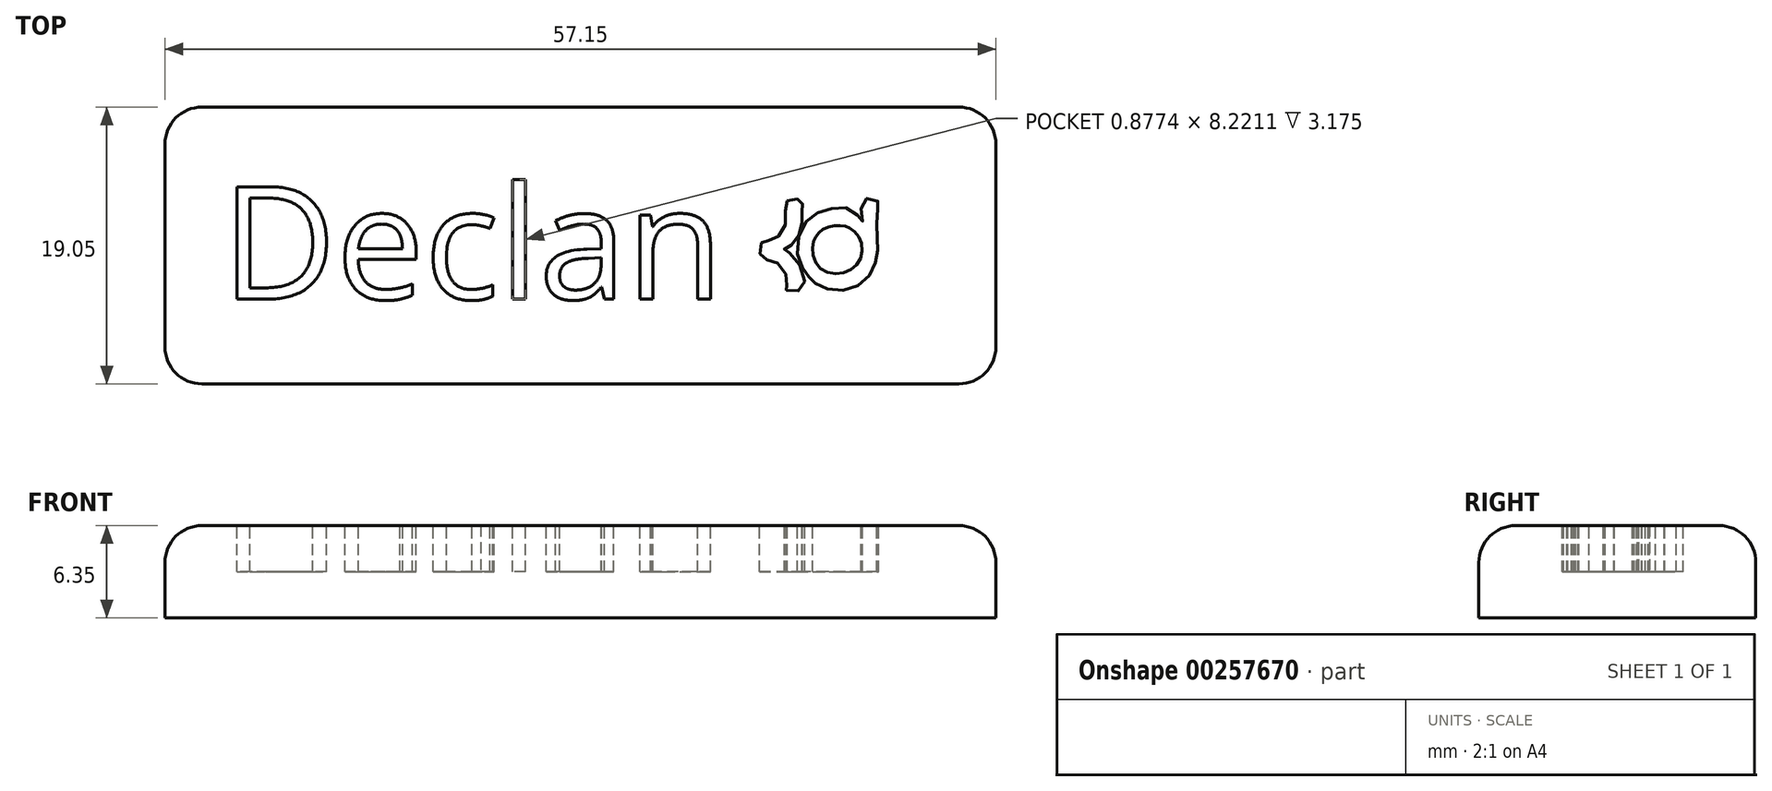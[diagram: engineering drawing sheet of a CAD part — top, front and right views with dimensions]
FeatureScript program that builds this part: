
annotation { "Feature Type Name" : "Feature", "Feature Type Description" : "" }
export const myFeature = defineFeature(function(context is Context, id is Id, definition is map)
    precondition{}
    {
        {
            var Q0;
            Q0=qCreatedBy(makeId("Top.planeOp"),FACE);
            var sketch = newSketch(context, id + "F0", { "sketchPlane" : qUnion([Q0])});
            skLineSegment(sketch, "E0.bottom", {"start": v(-25.12, 16.61) * mm, "end": v(32.03, 16.61) * mm});
            skLineSegment(sketch, "E0.top", {"start": v(-25.12, -2.44) * mm, "end": v(32.03, -2.44) * mm});
            skLineSegment(sketch, "E0.left", {"start": v(-25.12, 16.61) * mm, "end": v(-25.12, -2.44) * mm});
            skLineSegment(sketch, "E0.right", {"start": v(32.03, 16.61) * mm, "end": v(32.03, -2.44) * mm});
            skSolve(sketch);
        }
        {
            var Q0;
            Q0=makeQuery(id+"F0.imprint","IMPRINT",FACE,{"disambiguationData":[TD([[makeQuery(id+"F0.imprint","IMPRINT",EDGE,{"derivedFrom":sQuery(id+"F0.wireOp",EDGE,"E0.bottom")}),-1.0]])]});
            extrude(context, id + "F1", {"entities" : qUnion([Q0]), "depth" : 6.35 * mm});
        }
        {
            var Q0;
            Q0=makeQuery(id+"F1.opExtrude","CAP_EDGE",EDGE,{"disambiguationData":[OSD([sQuery(id+"F0.wireOp",EDGE,"E0.bottom")])],"isStart":false});
            fillet(context, id + "F2", {"entities" : qUnion([Q0]), "radius" : 2.54 * mm, "tangentPropagation" : true, "allowEdgeOverflow" : false});
        }
        {
            var Q0;
            Q0=makeQuery(id+"F1.opExtrude","CAP_EDGE",EDGE,{"disambiguationData":[OSD([sQuery(id+"F0.wireOp",EDGE,"E0.top")])],"isStart":false});
            fillet(context, id + "F3", {"entities" : qUnion([Q0]), "radius" : 2.54 * mm, "tangentPropagation" : true, "allowEdgeOverflow" : false});
        }
        {
            var Q0;
            Q0=makeQuery(id+"F1.opExtrude","CAP_EDGE",EDGE,{"disambiguationData":[OSD([sQuery(id+"F0.wireOp",EDGE,"E0.left")])],"isStart":false});
            fillet(context, id + "F4", {"entities" : qUnion([Q0]), "radius" : 2.54 * mm, "tangentPropagation" : true, "allowEdgeOverflow" : false});
        }
        {
            var Q0;
            Q0=makeQuery(id+"F1.opExtrude","CAP_EDGE",EDGE,{"disambiguationData":[OSD([sQuery(id+"F0.wireOp",EDGE,"E0.right")])],"isStart":false});
            fillet(context, id + "F5", {"entities" : qUnion([Q0]), "radius" : 2.54 * mm, "tangentPropagation" : true, "allowEdgeOverflow" : false});
        }
        {
            var Q0;
            Q0=makeQuery(id+"F1.opExtrude","CAP_FACE",FACE,{"disambiguationData":[OSD([sQuery(id+"F0.wireOp",EDGE,"E0.bottom"),sQuery(id+"F0.wireOp",EDGE,"E0.top"),sQuery(id+"F0.wireOp",EDGE,"E0.left"),sQuery(id+"F0.wireOp",EDGE,"E0.right")])],"isStart":false});
            var sketch = newSketch(context, id + "F6", { "sketchPlane" : qUnion([Q0])});
            skFitSpline(sketch, "E1", {"points": [v(17.67, 10.16) * mm, v(18.66, 10.16) * mm, v(18.7, 9.72) * mm, v(18.7, 8.75) * mm, v(18.05, 7.18) * mm, v(17.48, 6.83) * mm, v(18.09, 6.35) * mm, v(18.73, 4.1) * mm, v(17.54, 4.08) * mm, v(17.67, 4.43) * mm, v(17.03, 5.87) * mm, v(15.94, 6.25) * mm, v(15.94, 7.31) * mm, v(16.68, 7.47) * mm, v(17.57, 8.7) * mm, v(17.67, 10.16) * mm]});
            skFitSpline(sketch, "E2", {"points": [v(23.89, 9.59) * mm, v(23.85, 7.66) * mm, v(23.85, 6.41) * mm, v(23.18, 4.84) * mm, v(21.29, 3.98) * mm, v(19.62, 4.5) * mm, v(19.11, 5) * mm, v(18.4, 6.35) * mm, v(18.98, 8.75) * mm, v(20.58, 9.59) * mm, v(22.22, 9.46) * mm, v(22.86, 8.75) * mm, v(22.86, 10.16) * mm, v(23.89, 10.16) * mm, v(23.89, 9.59) * mm]});
            skPoint(sketch, "E3.6.internal.snap0", {"position": v(24.93, 7.1) * mm});
            skFitSpline(sketch, "E3", {"points": [v(21.32, 8.47) * mm, v(21.96, 8.3) * mm, v(22.7, 7.47) * mm, v(22.64, 6.03) * mm, v(21.35, 5.17) * mm, v(19.82, 5.65) * mm, v(19.43, 7.1) * mm, v(19.75, 7.82) * mm, v(20.33, 8.3) * mm, v(21.32, 8.47) * mm]});
            skSolve(sketch);
        }
        {
            var Q0;
            Q0 = qSketchRegion(id + "F6", true);
            extrude(context, id + "F7", {"entities" : qUnion([Q0]), "operationType" : NewBodyOperationType.REMOVE, "oppositeDirection" : true, "depth" : 3.17 * mm});
        }
        {
            var Q0;
            {var subQ0=sQuery(id+"F0.wireOp",EDGE,"E0.left");var subQ2=sQuery(id+"F0.wireOp",EDGE,"E0.top");var subQ4=sQuery(id+"F0.wireOp",EDGE,"E0.bottom");var subQ6=sQuery(id+"F0.wireOp",EDGE,"E0.right");Q0=makeQuery(id+"F7.boolean.opBoolean","SPLIT",FACE,{"disambiguationData":[TD([makeQuery(id+"F2.opFillet","BLEND_FACE",FACE,{"disambiguationData":[OSD([subQ4])]})])],"derivedFrom":makeQuery(id+"F1.opExtrude","CAP_FACE",FACE,{"disambiguationData":[OSD([subQ4,subQ2,subQ0,subQ6])],"isStart":false})});}
            var sketch = newSketch(context, id + "F8", { "sketchPlane" : qUnion([Q0])});
            skText(sketch, "E4", { "text": "Declan", "fontName": "OpenSans-Regular.ttf"});
            const initialGuessF8  = {"E4": [-0.02124, 0.0034, 1, 0, 0.00779]};
            skSetInitialGuess(sketch, initialGuessF8);
            skSolve(sketch);
        }
        {
            var Q0;
            Q0 = qSketchRegion(id + "F8", true);
            extrude(context, id + "F9", {"entities" : qUnion([Q0]), "operationType" : NewBodyOperationType.REMOVE, "oppositeDirection" : true, "depth" : 3.17 * mm});
        }
    });
